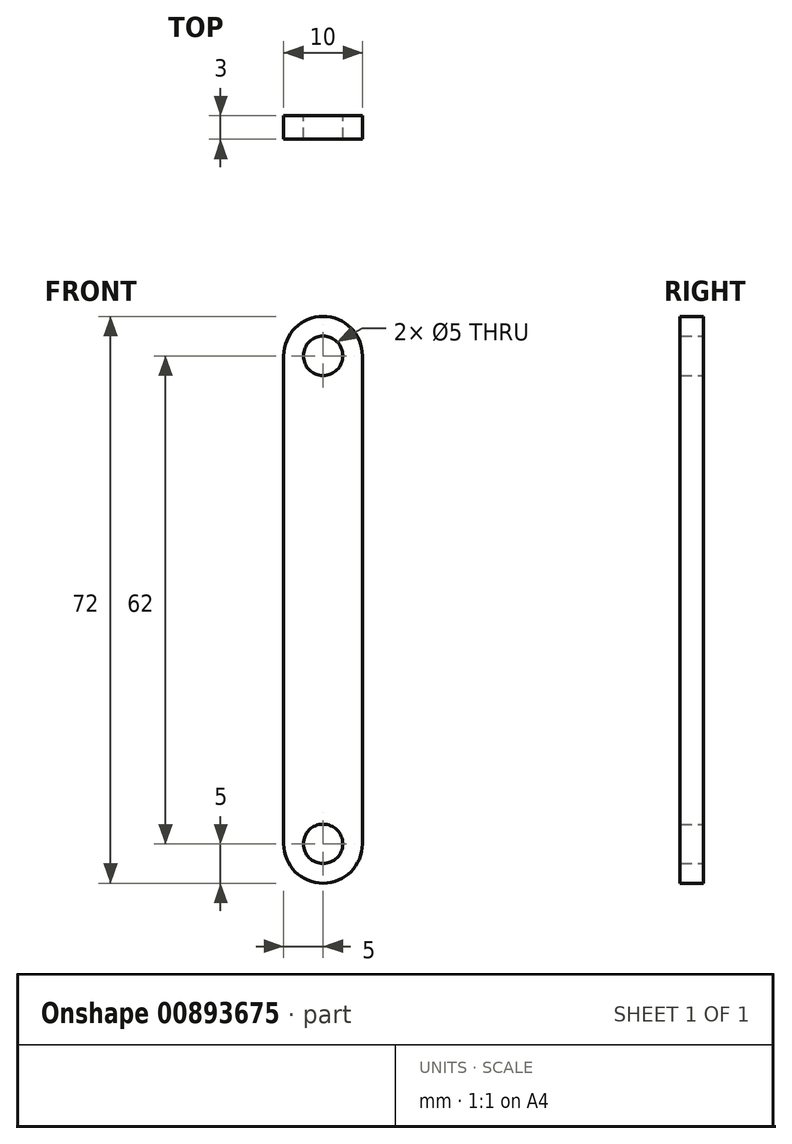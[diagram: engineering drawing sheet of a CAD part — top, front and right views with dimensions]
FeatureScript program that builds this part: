
annotation { "Feature Type Name" : "Feature", "Feature Type Description" : "" }
export const myFeature = defineFeature(function(context is Context, id is Id, definition is map)
    precondition{}
    {
        {
            var Q0;
            Q0=qCreatedBy(makeId("Front.planeOp"),FACE);
            var sketch = newSketch(context, id + "F0", { "sketchPlane" : qUnion([Q0])});
            skLineSegment(sketch, "E0.left", {"start": v(5, -31) * mm, "end": v(5, 31) * mm});
            skLineSegment(sketch, "E0.right", {"start": v(-5, -31) * mm, "end": v(-5, 31) * mm});
            skPoint(sketch, "E0.middle", {"position": v(0, 0) * mm});
            skArc(sketch, "E1", {"start": v(5, 31) * mm, "mid": v(0, 36) * mm, "end": v(-5, 31) * mm});
            skArc(sketch, "E2", {"start": v(-5, -31) * mm, "mid": v(0, -36) * mm, "end": v(5, -31) * mm});
            skCircle(sketch, "E3", {"center": v(0, 31) * mm, "radius": 2.5 * mm});
            skCircle(sketch, "E4", {"center": v(0, -31) * mm, "radius": 2.5 * mm});
            skSolve(sketch);
        }
        {
            var Q0;
            Q0 = qSketchRegion(id + "F0", true);
            extrude(context, id + "F1", {"entities" : qUnion([Q0]), "depth" : 3 * mm, "offsetDistance" : 25 * mm});
        }
    });
